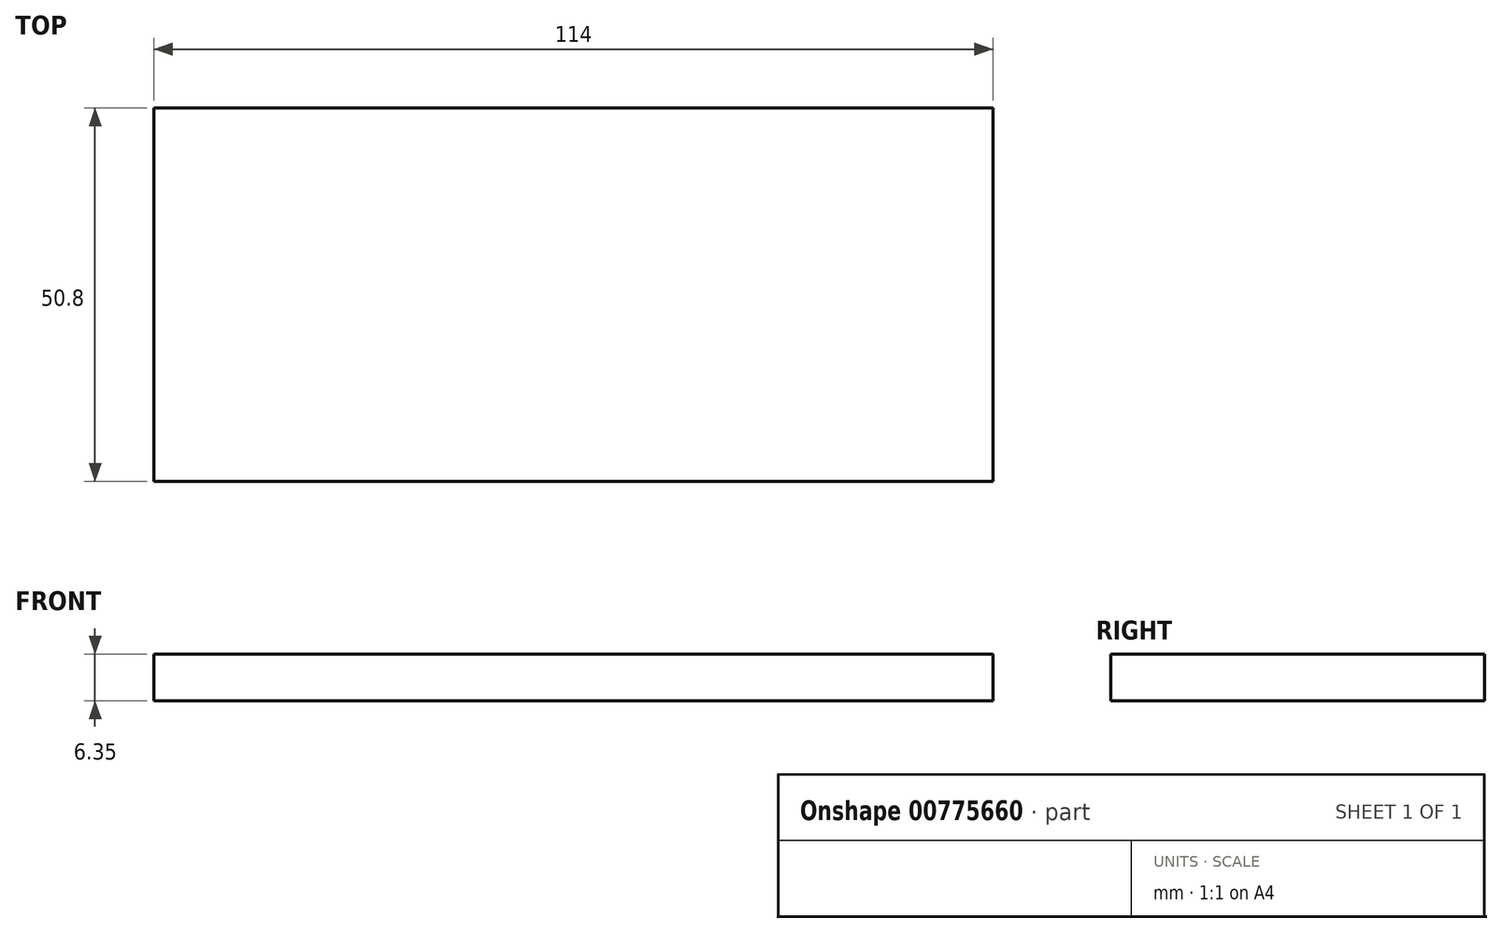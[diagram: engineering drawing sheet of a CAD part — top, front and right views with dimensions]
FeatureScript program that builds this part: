
annotation { "Feature Type Name" : "Feature", "Feature Type Description" : "" }
export const myFeature = defineFeature(function(context is Context, id is Id, definition is map)
    precondition{}
    {
        {
            var Q0;
            Q0=qCreatedBy(makeId("Top.planeOp"),FACE);
            var sketch = newSketch(context, id + "F0", { "sketchPlane" : qUnion([Q0])});
            skLineSegment(sketch, "E0.bottom", {"start": v(57, -25.4) * mm, "end": v(-57, -25.4) * mm});
            skLineSegment(sketch, "E0.top", {"start": v(57, 25.4) * mm, "end": v(-57, 25.4) * mm});
            skLineSegment(sketch, "E0.left", {"start": v(57, -25.4) * mm, "end": v(57, 25.4) * mm});
            skLineSegment(sketch, "E0.right", {"start": v(-57, -25.4) * mm, "end": v(-57, 25.4) * mm});
            skPoint(sketch, "E0.middle", {"position": v(0, 0) * mm});
            skSolve(sketch);
        }
        {
            var Q0;
            Q0=makeQuery(id+"F0.imprint","IMPRINT",FACE,{"disambiguationData":[TD([[makeQuery(id+"F0.imprint","IMPRINT",EDGE,{"derivedFrom":sQuery(id+"F0.wireOp",EDGE,"E0.bottom")}),-1.0]])]});
            extrude(context, id + "F1", {"entities" : qUnion([Q0]), "depth" : 6.35 * mm, "offsetDistance" : 25 * mm});
        }
    });
